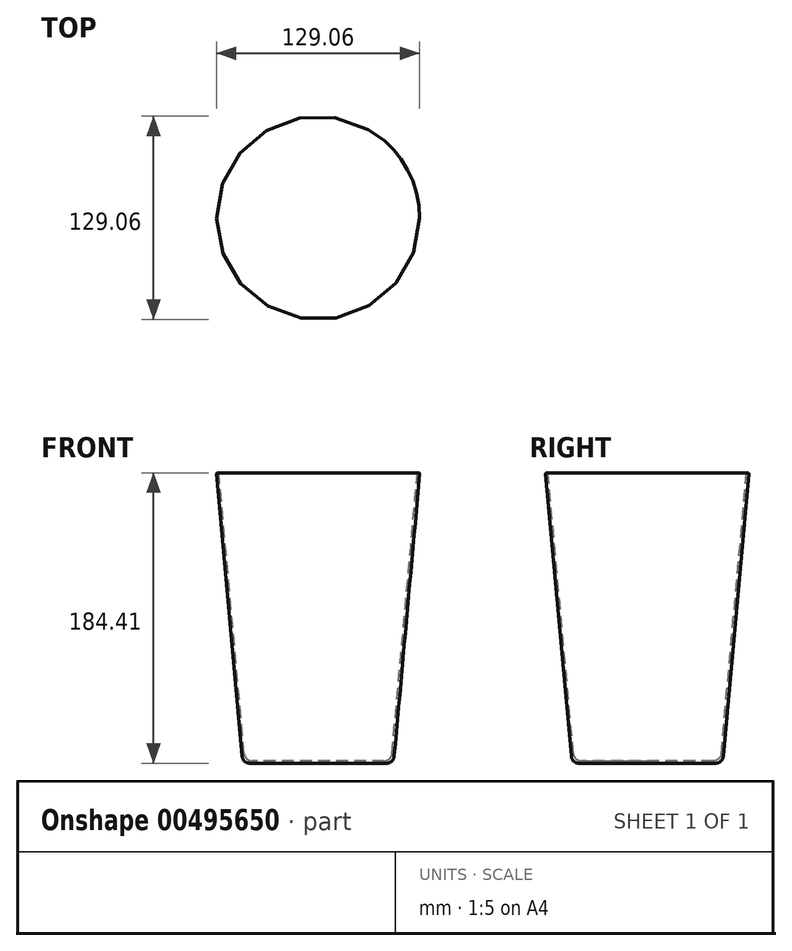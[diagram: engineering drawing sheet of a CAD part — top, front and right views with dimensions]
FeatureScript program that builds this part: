
annotation { "Feature Type Name" : "Feature", "Feature Type Description" : "" }
export const myFeature = defineFeature(function(context is Context, id is Id, definition is map)
    precondition{}
    {
        {
            var Q0;
            Q0=qCreatedBy(makeId("Front.planeOp"),FACE);
            var sketch = newSketch(context, id + "F0", { "sketchPlane" : qUnion([Q0])});
            skLineSegment(sketch, "E0", {"start": v(0, 0) * mm, "end": v(-43.33, 0) * mm});
            skLineSegment(sketch, "E1", {"start": v(-64.52, 183.82) * mm, "end": v(-48.3, 4.55) * mm});
            skLineSegment(sketch, "E2.0", {"start": v(-63.03, 183.95) * mm, "end": v(-46.94, 6.05) * mm});
            skLineSegment(sketch, "E3.0", {"start": v(0, 1.5) * mm, "end": v(-41.96, 1.5) * mm});
            skLineSegment(sketch, "E4", {"start": v(0, 1.5) * mm, "end": v(0, 0) * mm});
            skLineSegment(sketch, "E5", {"start": v(-64.07, 184.36) * mm, "end": v(-63.57, 184.4) * mm});
            skPoint(sketch, "E6.visualSharp", {"position": v(-63.07, 184.45) * mm});
            skArc(sketch, "E6.filletArc", {"start": v(-63.03, 183.95) * mm, "mid": v(-63.2, 184.3) * mm, "end": v(-63.57, 184.4) * mm});
            skPoint(sketch, "E7.visualSharp", {"position": v(-64.57, 184.32) * mm});
            skArc(sketch, "E7.filletArc", {"start": v(-64.07, 184.36) * mm, "mid": v(-64.4, 184.18) * mm, "end": v(-64.52, 183.82) * mm});
            skPoint(sketch, "E8.visualSharp", {"position": v(-47.9, 0) * mm});
            skArc(sketch, "E8.filletArc", {"start": v(-48.3, 4.55) * mm, "mid": v(-46.7, 1.3) * mm, "end": v(-43.33, 0) * mm});
            skPoint(sketch, "E9.visualSharp", {"position": v(-46.53, 1.5) * mm});
            skArc(sketch, "E9.filletArc", {"start": v(-46.94, 6.05) * mm, "mid": v(-45.33, 2.8) * mm, "end": v(-41.96, 1.5) * mm});
            skSolve(sketch);
        }
        {
            var Q0;
            Q0=makeQuery(id+"F0.imprint","IMPRINT",FACE,{"disambiguationData":[TD([[makeQuery(id+"F0.imprint","IMPRINT",EDGE,{"derivedFrom":sQuery(id+"F0.wireOp",EDGE,"E0")}),-1.0]])]});
            var Q1;
            Q1=sQuery(id+"F0.wireOp",EDGE,"E4");
            revolve(context, id + "F1", {"entities" : qUnion([Q0]), "axis" : qUnion([Q1]), "revolveType" : RevolveType.FULL});
        }
    });
